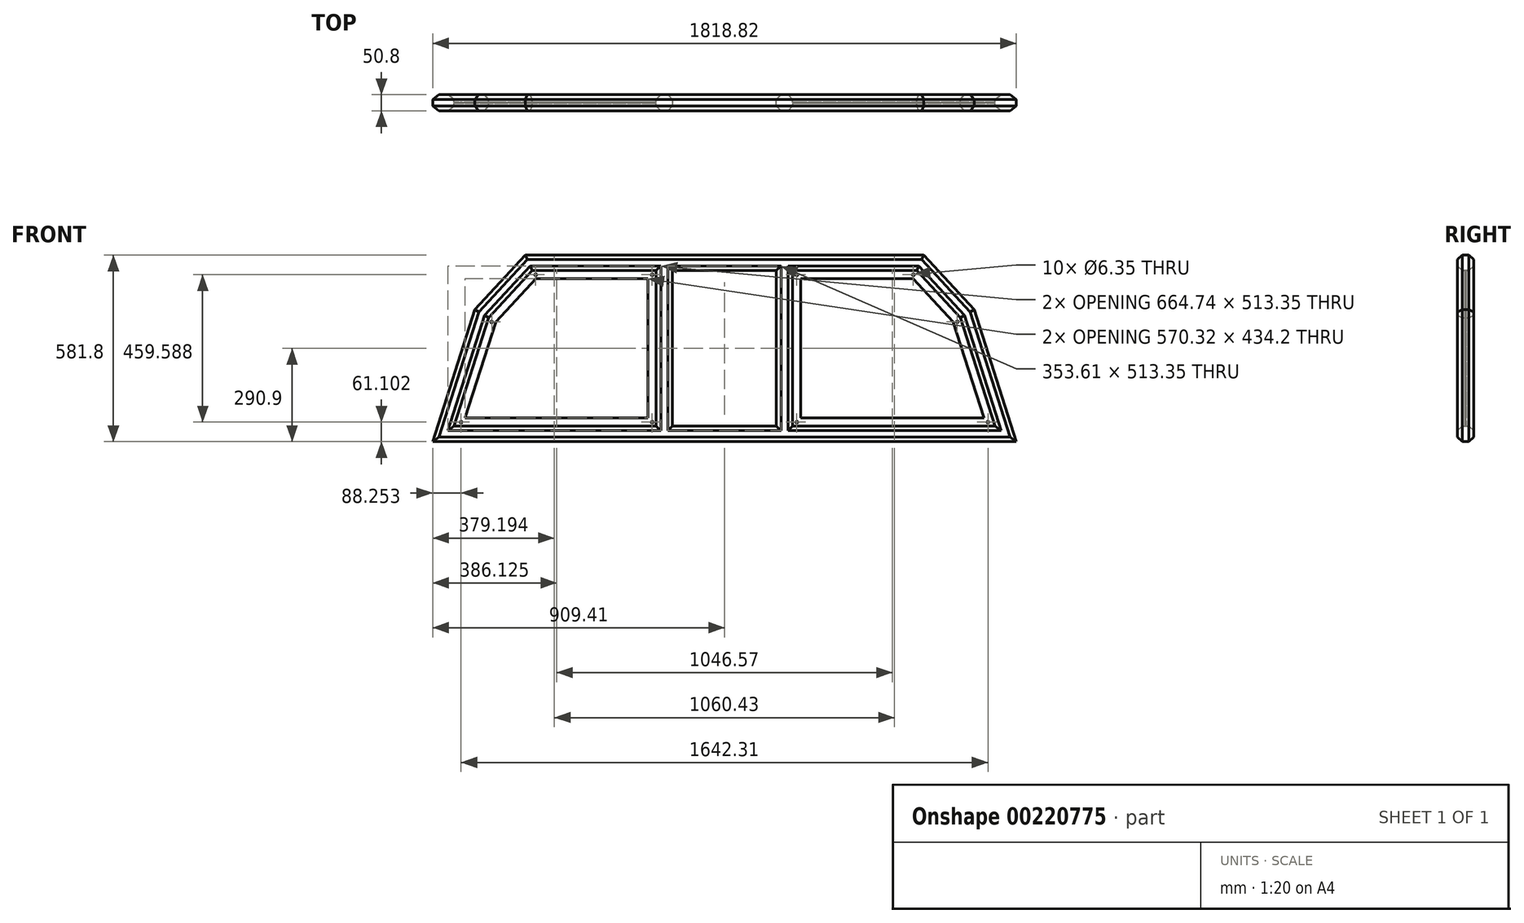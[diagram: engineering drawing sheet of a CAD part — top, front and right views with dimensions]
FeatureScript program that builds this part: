
annotation { "Feature Type Name" : "Feature", "Feature Type Description" : "" }
export const myFeature = defineFeature(function(context is Context, id is Id, definition is map)
    precondition{}
    {
        {
            var Q0;
            Q0=qCreatedBy(makeId("Front.planeOp"),FACE);
            var sketch = newSketch(context, id + "F0", { "sketchPlane" : qUnion([Q0])});
            skLineSegment(sketch, "E0", {"start": v(0, 0) * mm, "end": v(0, -743.78) * mm});
            skLineSegment(sketch, "E1", {"start": v(0, 0) * mm, "end": v(-876.3, 0) * mm});
            skLineSegment(sketch, "E2", {"start": v(-876.3, 0) * mm, "end": v(-756.83, 375.13) * mm});
            skLineSegment(sketch, "E3", {"start": v(-756.83, 375.13) * mm, "end": v(-609.98, 533.4) * mm});
            skLineSegment(sketch, "E4", {"start": v(-609.98, 533.4) * mm, "end": v(0, 533.4) * mm});
            skLineSegment(sketch, "E5", {"start": v(-187.33, 533.4) * mm, "end": v(-187.33, 0) * mm});
            skLineSegment(sketch, "E6.MirrorCS", {"start": v(0, 0) * mm, "end": v(876.3, 0) * mm});
            skLineSegment(sketch, "E7.MirrorCS", {"start": v(876.3, 0) * mm, "end": v(756.83, 375.13) * mm});
            skLineSegment(sketch, "E8.MirrorCS", {"start": v(187.32, 533.4) * mm, "end": v(187.32, 0) * mm});
            skLineSegment(sketch, "E9.MirrorCS", {"start": v(756.83, 375.13) * mm, "end": v(609.98, 533.4) * mm});
            skLineSegment(sketch, "E10.MirrorCS", {"start": v(609.98, 533.4) * mm, "end": v(0, 533.4) * mm});
            skSolve(sketch);
        }
        {
            var Q0;
            Q0=qCreatedBy(makeId("Top.planeOp"),FACE);
            var sketch = newSketch(context, id + "F1", { "sketchPlane" : qUnion([Q0])});
            skCircle(sketch, "E11.cCircle", {"center": v(876.3, 0) * mm, "radius": 25.4 * mm, "construction": true});
            skLineSegment(sketch, "E11.0", {"start": v(865.78, 25.4) * mm, "end": v(886.82, 25.4) * mm});
            skLineSegment(sketch, "E11.1", {"start": v(886.82, 25.4) * mm, "end": v(901.7, 10.52) * mm});
            skLineSegment(sketch, "E11.2", {"start": v(901.7, 10.52) * mm, "end": v(901.7, -10.52) * mm});
            skLineSegment(sketch, "E11.3", {"start": v(901.7, -10.52) * mm, "end": v(886.82, -25.4) * mm});
            skLineSegment(sketch, "E11.4", {"start": v(886.82, -25.4) * mm, "end": v(865.78, -25.4) * mm});
            skLineSegment(sketch, "E11.5", {"start": v(865.78, -25.4) * mm, "end": v(850.9, -10.52) * mm});
            skLineSegment(sketch, "E11.6", {"start": v(850.9, -10.52) * mm, "end": v(850.9, 10.52) * mm});
            skLineSegment(sketch, "E11.7", {"start": v(850.9, 10.52) * mm, "end": v(865.78, 25.4) * mm});
            skPoint(sketch, "E11.0.midPoint", {"position": v(876.3, 25.4) * mm});
            skSolve(sketch);
        }
        {
            var Q0;
            Q0=makeQuery(id+"F1.imprint","IMPRINT",FACE,{"disambiguationData":[TD([[makeQuery(id+"F1.imprint","IMPRINT",EDGE,{"derivedFrom":sQuery(id+"F1.wireOp",EDGE,"E11.0")}),-1.0]])]});
            var Q1;
            Q1=sQuery(id+"F0.wireOp",EDGE,"E7.MirrorCS");
            var Q2;
            Q2=sQuery(id+"F0.wireOp",EDGE,"E9.MirrorCS");
            var Q3;
            Q3=sQuery(id+"F0.wireOp",EDGE,"E10.MirrorCS");
            var Q4;
            Q4=sQuery(id+"F0.wireOp",EDGE,"E4");
            var Q5;
            Q5=sQuery(id+"F0.wireOp",EDGE,"E3");
            var Q6;
            Q6=sQuery(id+"F0.wireOp",EDGE,"E2");
            var Q7;
            Q7=sQuery(id+"F0.wireOp",EDGE,"E1");
            var Q8;
            Q8=sQuery(id+"F0.wireOp",EDGE,"E6.MirrorCS");
            sweep(context, id + "F2", {"profiles" : qUnion([Q0]), "path" : qUnion([Q1, Q2, Q3, Q4, Q5, Q6, Q7, Q8])});
        }
        {
            var Q0;
            Q0=qCreatedBy(makeId("Top.planeOp"),FACE);
            var sketch = newSketch(context, id + "F3", { "sketchPlane" : qUnion([Q0])});
            skCircle(sketch, "E12.cCircle", {"center": v(187.32, 0) * mm, "radius": 25.4 * mm, "construction": true});
            skLineSegment(sketch, "E12.0", {"start": v(176.8, 25.4) * mm, "end": v(197.85, 25.4) * mm});
            skLineSegment(sketch, "E12.1", {"start": v(197.85, 25.4) * mm, "end": v(212.72, 10.52) * mm});
            skLineSegment(sketch, "E12.2", {"start": v(212.72, 10.52) * mm, "end": v(212.72, -10.52) * mm});
            skLineSegment(sketch, "E12.3", {"start": v(212.72, -10.52) * mm, "end": v(197.85, -25.4) * mm});
            skLineSegment(sketch, "E12.4", {"start": v(197.85, -25.4) * mm, "end": v(176.8, -25.4) * mm});
            skLineSegment(sketch, "E12.5", {"start": v(176.8, -25.4) * mm, "end": v(161.92, -10.52) * mm});
            skLineSegment(sketch, "E12.6", {"start": v(161.92, -10.52) * mm, "end": v(161.92, 10.52) * mm});
            skLineSegment(sketch, "E12.7", {"start": v(161.92, 10.52) * mm, "end": v(176.8, 25.4) * mm});
            skPoint(sketch, "E12.0.midPoint", {"position": v(187.32, 25.4) * mm});
            skCircle(sketch, "E13.cCircle", {"center": v(-187.33, 0) * mm, "radius": 25.4 * mm, "construction": true});
            skLineSegment(sketch, "E13.0", {"start": v(-197.85, 25.4) * mm, "end": v(-176.8, 25.4) * mm});
            skLineSegment(sketch, "E13.1", {"start": v(-176.8, 25.4) * mm, "end": v(-161.92, 10.52) * mm});
            skLineSegment(sketch, "E13.2", {"start": v(-161.92, 10.52) * mm, "end": v(-161.92, -10.52) * mm});
            skLineSegment(sketch, "E13.3", {"start": v(-161.93, -10.52) * mm, "end": v(-176.8, -25.4) * mm});
            skLineSegment(sketch, "E13.4", {"start": v(-176.8, -25.4) * mm, "end": v(-197.85, -25.4) * mm});
            skLineSegment(sketch, "E13.5", {"start": v(-197.85, -25.4) * mm, "end": v(-212.72, -10.52) * mm});
            skLineSegment(sketch, "E13.6", {"start": v(-212.73, -10.52) * mm, "end": v(-212.73, 10.52) * mm});
            skLineSegment(sketch, "E13.7", {"start": v(-212.72, 10.52) * mm, "end": v(-197.85, 25.4) * mm});
            skPoint(sketch, "E13.0.midPoint", {"position": v(-187.33, 25.4) * mm});
            skSolve(sketch);
        }
        {
            var Q0;
            Q0=makeQuery(id+"F3.imprint","IMPRINT",FACE,{"disambiguationData":[TD([[makeQuery(id+"F3.imprint","IMPRINT",EDGE,{"derivedFrom":sQuery(id+"F3.wireOp",EDGE,"E12.0")}),-1.0]])]});
            var Q1;
            Q1=sQuery(id+"F0.wireOp",EDGE,"E8.MirrorCS");
            sweep(context, id + "F4", {"profiles" : qUnion([Q0]), "path" : qUnion([Q1])});
        }
        {
            var Q0;
            Q0=makeQuery(id+"F3.imprint","IMPRINT",FACE,{"disambiguationData":[TD([[makeQuery(id+"F3.imprint","IMPRINT",EDGE,{"derivedFrom":sQuery(id+"F3.wireOp",EDGE,"E13.0")}),-1.0]])]});
            var Q1;
            Q1=sQuery(id+"F0.wireOp",EDGE,"E5");
            sweep(context, id + "F5", {"profiles" : qUnion([Q0]), "path" : qUnion([Q1])});
        }
        {
            var Q0;
            Q0=qCreatedBy(makeId("Front.planeOp"),FACE);
            var sketch = newSketch(context, id + "F6", { "sketchPlane" : qUnion([Q0])});
            skLineSegment(sketch, "E14", {"start": v(-843.2, 24.2) * mm, "end": v(-212.72, 24.2) * mm});
            skLineSegment(sketch, "E15", {"start": v(-212.72, 24.2) * mm, "end": v(-212.73, 509.2) * mm});
            skLineSegment(sketch, "E16", {"start": v(-212.73, 509.2) * mm, "end": v(-599.42, 509.2) * mm});
            skLineSegment(sketch, "E17", {"start": v(-599.42, 509.2) * mm, "end": v(-735.4, 362.64) * mm});
            skLineSegment(sketch, "E18", {"start": v(-735.4, 362.64) * mm, "end": v(-843.2, 24.2) * mm});
            skLineSegment(sketch, "E19.0", {"start": v(-712.93, 349.52) * mm, "end": v(-808.45, 49.6) * mm});
            skLineSegment(sketch, "E19.1", {"start": v(-588.34, 483.8) * mm, "end": v(-712.93, 349.52) * mm});
            skLineSegment(sketch, "E19.2", {"start": v(-808.45, 49.6) * mm, "end": v(-238.12, 49.6) * mm});
            skLineSegment(sketch, "E19.3", {"start": v(-238.12, 49.6) * mm, "end": v(-238.13, 483.8) * mm});
            skLineSegment(sketch, "E19.4", {"start": v(-238.13, 483.8) * mm, "end": v(-588.34, 483.8) * mm});
            skLineSegment(sketch, "E20", {"start": v(0, 0) * mm, "end": v(0, -250.49) * mm});
            skLineSegment(sketch, "E21.MirrorCS", {"start": v(808.45, 49.6) * mm, "end": v(238.12, 49.6) * mm});
            skLineSegment(sketch, "E22.MirrorCS", {"start": v(843.2, 24.2) * mm, "end": v(212.72, 24.2) * mm});
            skLineSegment(sketch, "E23.MirrorCS", {"start": v(212.72, 24.2) * mm, "end": v(212.73, 509.2) * mm});
            skLineSegment(sketch, "E24.MirrorCS", {"start": v(238.12, 49.6) * mm, "end": v(238.13, 483.8) * mm});
            skLineSegment(sketch, "E25.MirrorCS", {"start": v(238.12, 483.8) * mm, "end": v(588.34, 483.8) * mm});
            skLineSegment(sketch, "E26.MirrorCS", {"start": v(212.72, 509.2) * mm, "end": v(599.42, 509.2) * mm});
            skLineSegment(sketch, "E27.MirrorCS", {"start": v(599.42, 509.2) * mm, "end": v(735.4, 362.64) * mm});
            skLineSegment(sketch, "E28.MirrorCS", {"start": v(588.34, 483.8) * mm, "end": v(712.93, 349.52) * mm});
            skLineSegment(sketch, "E29.MirrorCS", {"start": v(712.93, 349.52) * mm, "end": v(808.45, 49.6) * mm});
            skLineSegment(sketch, "E30.MirrorCS", {"start": v(735.4, 362.64) * mm, "end": v(843.2, 24.2) * mm});
            skSolve(sketch);
        }
        {
            var Q0;
            Q0 = qSketchRegion(id + "F6", true);
            extrude(context, id + "F7", {"entities" : qUnion([Q0]), "operationType" : NewBodyOperationType.ADD, "depth" : 1.59 * mm, "hasSecondDirection" : true, "secondDirectionOppositeDirection" : true, "secondDirectionDepth" : 1.59 * mm});
        }
        {
            var Q0;
            Q0=makeQuery(id+"F7.opExtrude","CAP_FACE",FACE,{"disambiguationData":[OSD([sQuery(id+"F6.wireOp",EDGE,"E14"),sQuery(id+"F6.wireOp",EDGE,"E15"),sQuery(id+"F6.wireOp",EDGE,"E16"),sQuery(id+"F6.wireOp",EDGE,"E17"),sQuery(id+"F6.wireOp",EDGE,"E18"),sQuery(id+"F6.wireOp",EDGE,"E19.0"),sQuery(id+"F6.wireOp",EDGE,"E19.1"),sQuery(id+"F6.wireOp",EDGE,"E19.2"),sQuery(id+"F6.wireOp",EDGE,"E19.3"),sQuery(id+"F6.wireOp",EDGE,"E19.4")])],"isStart":false});
            var sketch = newSketch(context, id + "F8", { "sketchPlane" : qUnion([Q0])});
            skCircle(sketch, "E31", {"center": v(-225.42, 36.9) * mm, "radius": 3.18 * mm});
            skCircle(sketch, "E32", {"center": v(-225.43, 496.49) * mm, "radius": 3.18 * mm});
            skCircle(sketch, "E33", {"center": v(-588.65, 496.49) * mm, "radius": 3.18 * mm});
            skCircle(sketch, "E34", {"center": v(-725.63, 349.52) * mm, "radius": 3.18 * mm});
            skCircle(sketch, "E35", {"center": v(-821.16, 36.9) * mm, "radius": 3.18 * mm});
            skLineSegment(sketch, "E36", {"start": v(0, 0) * mm, "end": v(0, -139.08) * mm});
            skCircle(sketch, "E37.MirrorC", {"center": v(225.42, 36.9) * mm, "radius": 3.18 * mm});
            skCircle(sketch, "E38.MirrorC", {"center": v(225.43, 496.49) * mm, "radius": 3.18 * mm});
            skCircle(sketch, "E39.MirrorC", {"center": v(588.65, 496.49) * mm, "radius": 3.18 * mm});
            skCircle(sketch, "E40.MirrorC", {"center": v(725.63, 349.52) * mm, "radius": 3.18 * mm});
            skCircle(sketch, "E41.MirrorC", {"center": v(821.16, 36.9) * mm, "radius": 3.18 * mm});
            skSolve(sketch);
        }
        {
            var Q0;
            Q0 = qSketchRegion(id + "F8", true);
            var Q1;
            Q1=makeQuery(id+"F7.opExtrude","CAP_FACE",FACE,{"disambiguationData":[OSD([sQuery(id+"F6.wireOp",EDGE,"E14"),sQuery(id+"F6.wireOp",EDGE,"E15"),sQuery(id+"F6.wireOp",EDGE,"E16"),sQuery(id+"F6.wireOp",EDGE,"E17"),sQuery(id+"F6.wireOp",EDGE,"E18"),sQuery(id+"F6.wireOp",EDGE,"E19.0"),sQuery(id+"F6.wireOp",EDGE,"E19.1"),sQuery(id+"F6.wireOp",EDGE,"E19.2"),sQuery(id+"F6.wireOp",EDGE,"E19.3"),sQuery(id+"F6.wireOp",EDGE,"E19.4")])],"isStart":true});
            extrude(context, id + "F9", {"entities" : qUnion([Q0]), "operationType" : NewBodyOperationType.REMOVE, "endBound" : BoundingType.UP_TO_SURFACE, "oppositeDirection" : true, "endBoundEntityFace" : qUnion([Q1]), "depth" : 25.4 * mm});
        }
    });
